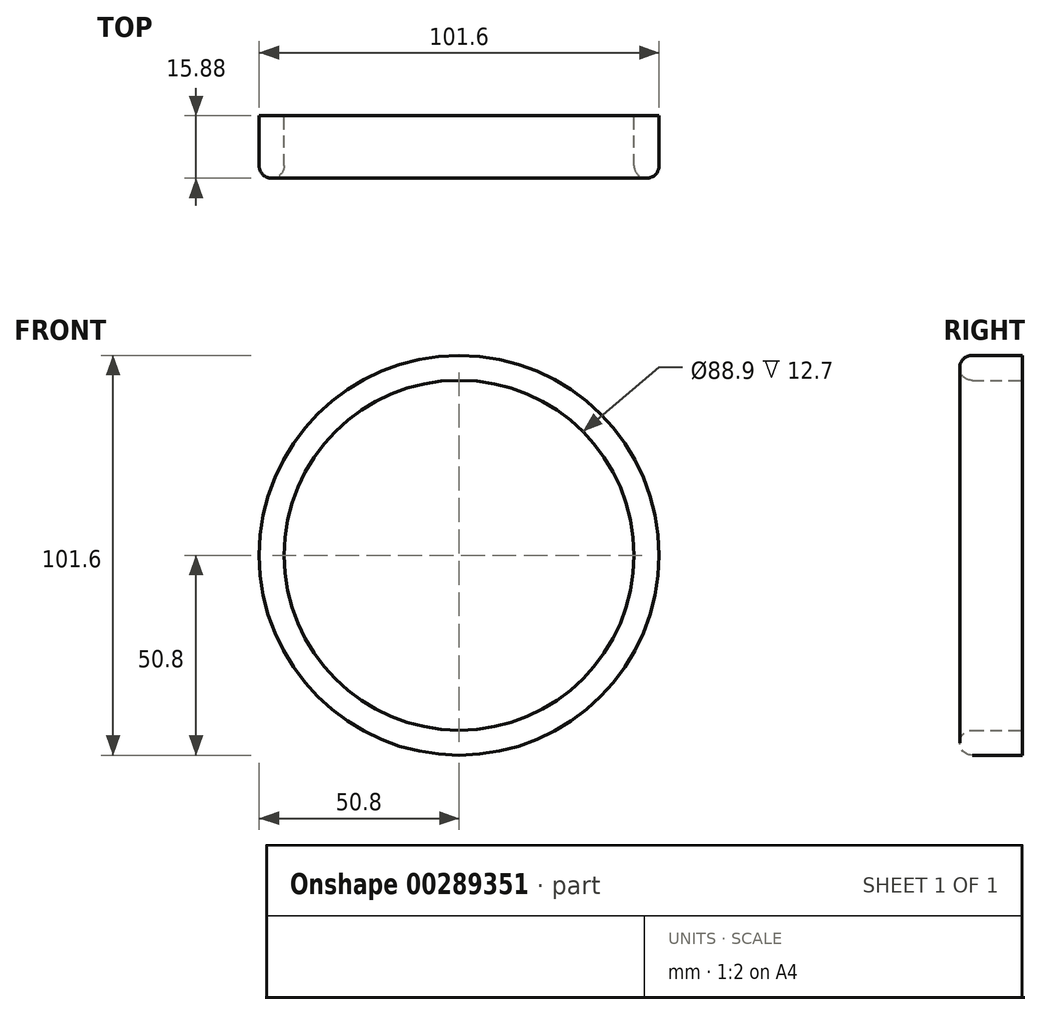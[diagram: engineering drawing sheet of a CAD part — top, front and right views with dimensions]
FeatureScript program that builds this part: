
annotation { "Feature Type Name" : "Feature", "Feature Type Description" : "" }
export const myFeature = defineFeature(function(context is Context, id is Id, definition is map)
    precondition{}
    {
        {
            var Q0;
            Q0=qCreatedBy(makeId("Front.planeOp"),FACE);
            var sketch = newSketch(context, id + "F0", { "sketchPlane" : qUnion([Q0])});
            skCircle(sketch, "E0", {"center": v(0, 0) * mm, "radius": 50.8 * mm});
            skSolve(sketch);
        }
        {
            var Q0;
            Q0 = qSketchRegion(id + "F0", true);
            extrude(context, id + "F1", {"entities" : qUnion([Q0]), "depth" : 15.88 * mm});
        }
        {
            var Q0;
            Q0=qCreatedBy(makeId("Front.planeOp"),FACE);
            var sketch = newSketch(context, id + "F2", { "sketchPlane" : qUnion([Q0])});
            skCircle(sketch, "E1", {"center": v(0, 0) * mm, "radius": 44.45 * mm});
            skSolve(sketch);
        }
        {
            var Q0;
            Q0=makeQuery(id+"F2.imprint","IMPRINT",FACE,{"disambiguationData":[TD([[makeQuery(id+"F2.imprint","IMPRINT",EDGE,{"derivedFrom":sQuery(id+"F2.wireOp",EDGE,"E1")}),1.0]])]});
            extrude(context, id + "F3", {"entities" : qUnion([Q0]), "operationType" : NewBodyOperationType.REMOVE, "endBound" : BoundingType.THROUGH_ALL, "depth" : 25.4 * mm});
        }
        {
            var Q0;
            Q0=makeQuery(id+"F1.opExtrude","CAP_EDGE",EDGE,{"disambiguationData":[OSD([sQuery(id+"F0.wireOp",EDGE,"E0")])],"isStart":false});
            var Q1;
            Q1=makeQuery(id+"F3.boolean.opBoolean","INTERSECT",EDGE,{"derivedFrom":[makeQuery(id+"F1.opExtrude","CAP_FACE",FACE,{"disambiguationData":[OSD([sQuery(id+"F0.wireOp",EDGE,"E0")])],"isStart":false}),makeQuery(id+"F3.opExtrude","SWEPT_FACE",FACE,{"disambiguationData":[OSD([sQuery(id+"F2.wireOp",EDGE,"E1")])]})]});
            fillet(context, id + "F4", {"entities" : qUnion([Q0, Q1]), "radius" : 3.17 * mm, "allowEdgeOverflow" : false});
        }
    });
